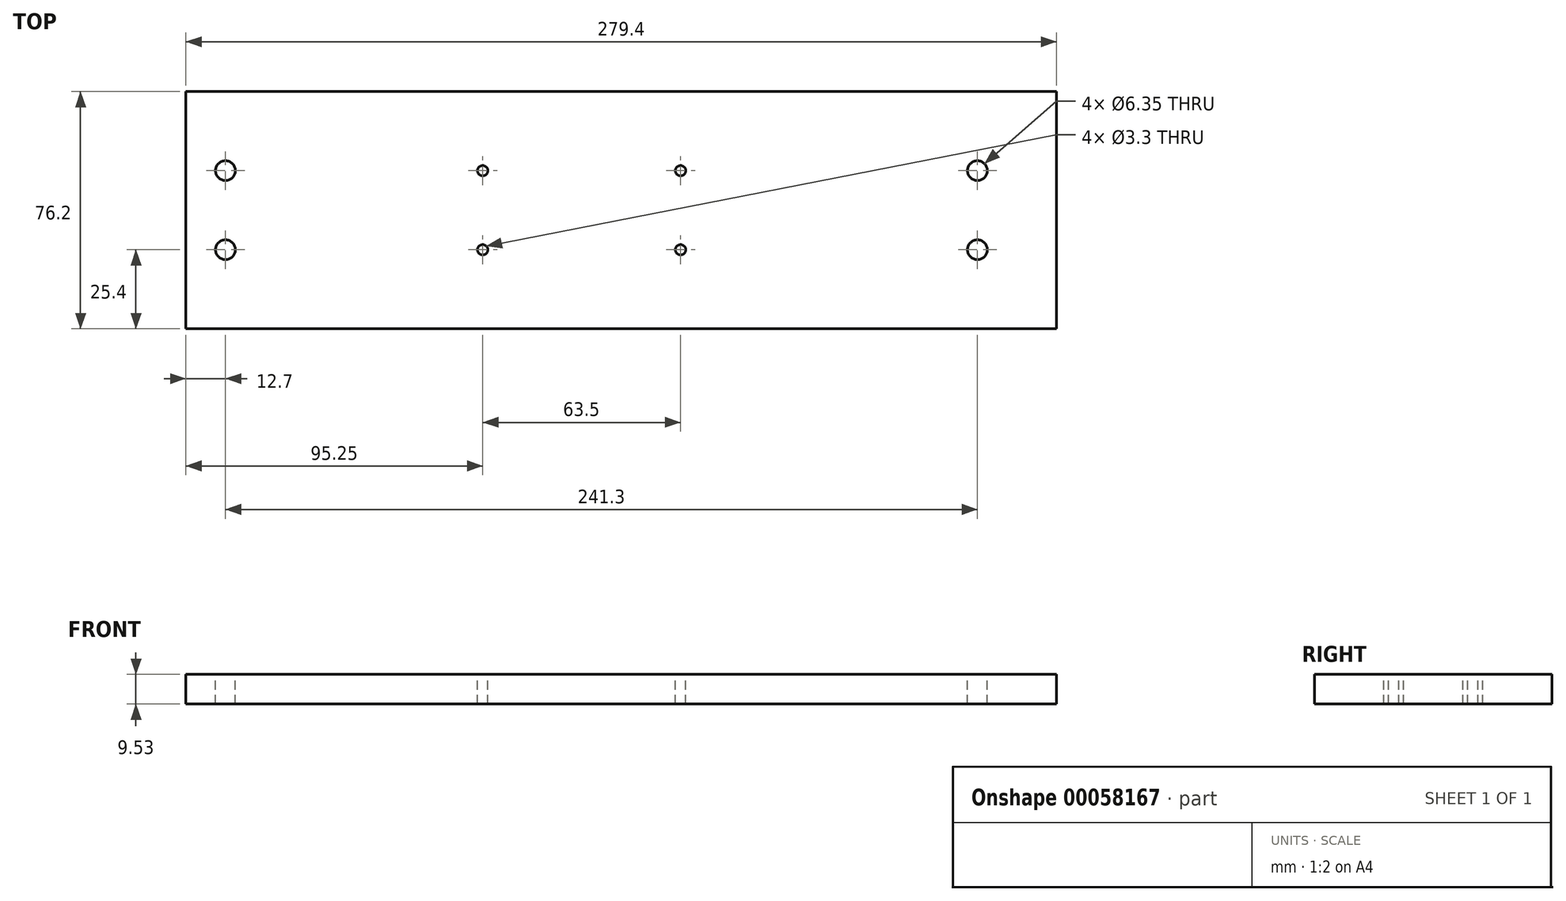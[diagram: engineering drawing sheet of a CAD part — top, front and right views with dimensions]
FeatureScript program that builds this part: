
annotation { "Feature Type Name" : "Feature", "Feature Type Description" : "" }
export const myFeature = defineFeature(function(context is Context, id is Id, definition is map)
    precondition{}
    {
        {
            var Q0;
            Q0=qCreatedBy(makeId("Top.planeOp"),FACE);
            var sketch = newSketch(context, id + "F0", { "sketchPlane" : qUnion([Q0])});
            skLineSegment(sketch, "E0.bottom", {"start": v(0, 0) * mm, "end": v(-279.4, 0) * mm});
            skLineSegment(sketch, "E0.top", {"start": v(0, -76.2) * mm, "end": v(-279.4, -76.2) * mm});
            skLineSegment(sketch, "E0.left", {"start": v(0, 0) * mm, "end": v(0, -76.2) * mm});
            skLineSegment(sketch, "E0.right", {"start": v(-279.4, 0) * mm, "end": v(-279.4, -76.2) * mm});
            skSolve(sketch);
        }
        {
            var Q0;
            Q0=makeQuery(id+"F0.imprint","IMPRINT",FACE,{"disambiguationData":[TD([[makeQuery(id+"F0.imprint","IMPRINT",EDGE,{"derivedFrom":sQuery(id+"F0.wireOp",EDGE,"E0.bottom")}),1.0]])]});
            extrude(context, id + "F1", {"entities" : qUnion([Q0]), "depth" : 9.52 * mm});
        }
        {
            var Q0;
            Q0=makeQuery(id+"F1.opExtrude","CAP_FACE",FACE,{"disambiguationData":[OSD([sQuery(id+"F0.wireOp",EDGE,"E0.bottom"),sQuery(id+"F0.wireOp",EDGE,"E0.top"),sQuery(id+"F0.wireOp",EDGE,"E0.left"),sQuery(id+"F0.wireOp",EDGE,"E0.right")])],"isStart":false});
            var sketch = newSketch(context, id + "F2", { "sketchPlane" : qUnion([Q0])});
            skCircle(sketch, "E1", {"center": v(-266.7, -25.4) * mm, "radius": 3.18 * mm});
            skCircle(sketch, "E2", {"center": v(-266.7, -50.8) * mm, "radius": 3.18 * mm});
            skCircle(sketch, "E3", {"center": v(-25.4, -25.4) * mm, "radius": 3.18 * mm});
            skCircle(sketch, "E4", {"center": v(-25.4, -50.8) * mm, "radius": 3.18 * mm});
            skCircle(sketch, "E5", {"center": v(-184.15, -50.8) * mm, "radius": 1.65 * mm});
            skCircle(sketch, "E6", {"center": v(-184.15, -25.4) * mm, "radius": 1.65 * mm});
            skCircle(sketch, "E7", {"center": v(-120.65, -50.8) * mm, "radius": 1.65 * mm});
            skCircle(sketch, "E8", {"center": v(-120.65, -25.4) * mm, "radius": 1.65 * mm});
            skSolve(sketch);
        }
        {
            var Q0;
            Q0=makeQuery(id+"F2.imprint","IMPRINT",FACE,{"disambiguationData":[TD([[makeQuery(id+"F2.imprint","IMPRINT",EDGE,{"derivedFrom":sQuery(id+"F2.wireOp",EDGE,"E1")}),1.0]])]});
            var Q1;
            Q1=makeQuery(id+"F2.imprint","IMPRINT",FACE,{"disambiguationData":[TD([[makeQuery(id+"F2.imprint","IMPRINT",EDGE,{"derivedFrom":sQuery(id+"F2.wireOp",EDGE,"E2")}),1.0]])]});
            var Q2;
            Q2=makeQuery(id+"F2.imprint","IMPRINT",FACE,{"disambiguationData":[TD([[makeQuery(id+"F2.imprint","IMPRINT",EDGE,{"derivedFrom":sQuery(id+"F2.wireOp",EDGE,"E4")}),1.0]])]});
            var Q3;
            Q3=makeQuery(id+"F2.imprint","IMPRINT",FACE,{"disambiguationData":[TD([[makeQuery(id+"F2.imprint","IMPRINT",EDGE,{"derivedFrom":sQuery(id+"F2.wireOp",EDGE,"E3")}),1.0]])]});
            var Q4;
            Q4=makeQuery(id+"F2.imprint","IMPRINT",FACE,{"disambiguationData":[TD([[makeQuery(id+"F2.imprint","IMPRINT",EDGE,{"derivedFrom":sQuery(id+"F2.wireOp",EDGE,"E7")}),1.0]])]});
            var Q5;
            Q5=makeQuery(id+"F2.imprint","IMPRINT",FACE,{"disambiguationData":[TD([[makeQuery(id+"F2.imprint","IMPRINT",EDGE,{"derivedFrom":sQuery(id+"F2.wireOp",EDGE,"E8")}),1.0]])]});
            var Q6;
            Q6=makeQuery(id+"F2.imprint","IMPRINT",FACE,{"disambiguationData":[TD([[makeQuery(id+"F2.imprint","IMPRINT",EDGE,{"derivedFrom":sQuery(id+"F2.wireOp",EDGE,"E5")}),1.0]])]});
            var Q7;
            Q7=makeQuery(id+"F2.imprint","IMPRINT",FACE,{"disambiguationData":[TD([[makeQuery(id+"F2.imprint","IMPRINT",EDGE,{"derivedFrom":sQuery(id+"F2.wireOp",EDGE,"E6")}),1.0]])]});
            extrude(context, id + "F3", {"entities" : qUnion([Q0, Q1, Q2, Q3, Q4, Q5, Q6, Q7]), "operationType" : NewBodyOperationType.REMOVE, "oppositeDirection" : true, "depth" : 25.4 * mm});
        }
    });
